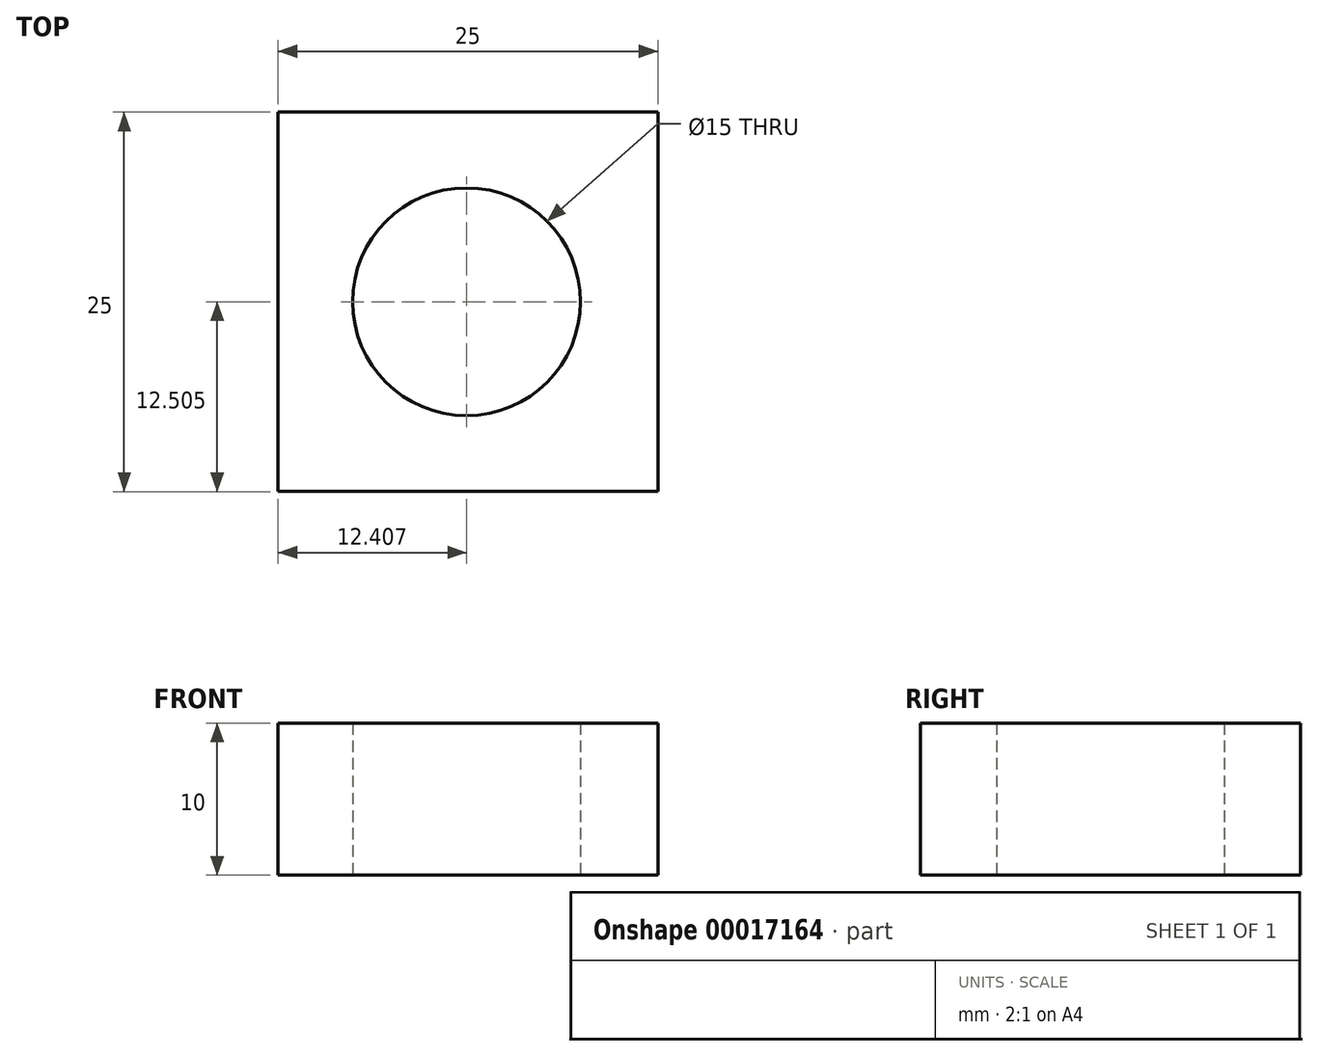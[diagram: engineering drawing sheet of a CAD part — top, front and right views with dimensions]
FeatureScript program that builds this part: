
annotation { "Feature Type Name" : "Feature", "Feature Type Description" : "" }
export const myFeature = defineFeature(function(context is Context, id is Id, definition is map)
    precondition{}
    {
        {
            var Q0;
            Q0=qCreatedBy(makeId("Top.planeOp"),FACE);
            var sketch = newSketch(context, id + "F0", { "sketchPlane" : qUnion([Q0])});
            skLineSegment(sketch, "E0.bottom", {"start": v(-7.51, 16.92) * mm, "end": v(17.49, 16.92) * mm});
            skLineSegment(sketch, "E0.top", {"start": v(-7.51, -8.08) * mm, "end": v(17.49, -8.08) * mm});
            skLineSegment(sketch, "E0.left", {"start": v(-7.51, 16.92) * mm, "end": v(-7.51, -8.08) * mm});
            skLineSegment(sketch, "E0.right", {"start": v(17.49, 16.92) * mm, "end": v(17.49, -8.08) * mm});
            skCircle(sketch, "E1", {"center": v(4.9, 4.42) * mm, "radius": 7.5 * mm});
            skSolve(sketch);
        }
        {
            var Q0;
            Q0 = qSketchRegion(id + "F0", true);
            extrude(context, id + "F1", {"entities" : qUnion([Q0]), "depth" : 10 * mm});
        }
    });
